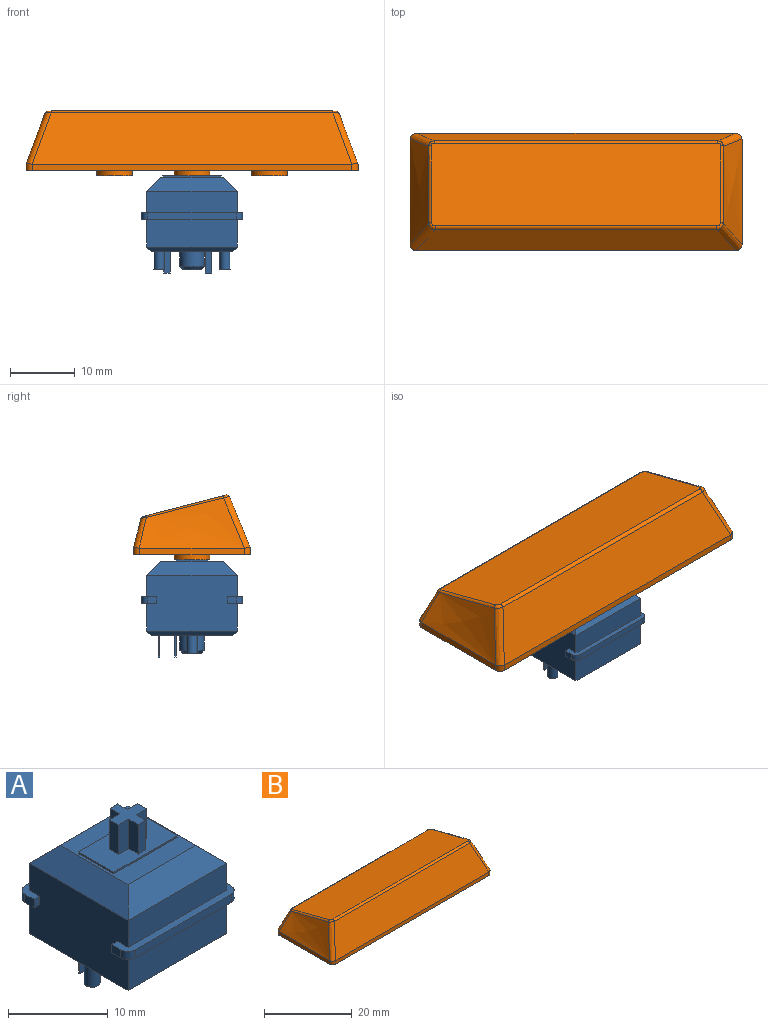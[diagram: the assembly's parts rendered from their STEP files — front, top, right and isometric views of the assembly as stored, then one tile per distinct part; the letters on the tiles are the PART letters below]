
ASSEMBLY  parts=2 mates=1
PART A: 69 faces, bbox 15.6x15.6x18.6 mm
  f0: plane 15.6x2.3mm, normal (0,0,-1), area 14.4mm2, adj f2,f3,f28,f30,f35,f60,f62,f63
  f1: plane 15.6x2.3mm, normal (0,0,-1), area 14.4mm2, adj f28,f30,f33,f34,f36,f59,f61,f64
  f2: plane 1.3x1mm, normal (1,0,0), area 1.3mm2, adj f0,f32,f62,f66
  f3: plane 1.3x1mm, normal (-1,0,0), area 1.3mm2, adj f0,f32,f63,f68
  f4: plane 15.6x2.3mm, normal (0,0,1), area 14.4mm2, adj f28,f30,f31,f33,f34,f36,f61,f64
  f5: plane 14x2.2mm, normal (-0.71,0,0.71), area 36.7mm2, adj f6,f7,f26,f30
  f6: plane 14x2.2mm, normal (0,-0.71,0.71), area 36.7mm2, adj f5,f7,f27,f31
  f7: plane 9.6x9.6mm, normal (0,0,1), area 47.2mm2, adj f5,f6,f8,f9,f10,f11,f26,f27
  f8: plane 5x0.2mm, normal (1,0,0), area 1mm2, adj f7,f9,f11,f12
  f9: plane 9x0.2mm, normal (0,1,0), area 1.8mm2, adj f7,f8,f10,f12
  f10: plane 5x0.2mm, normal (-1,0,0), area 1mm2, adj f7,f9,f11,f12
  f11: plane 9x0.2mm, normal (0,-1,0), area 1.8mm2, adj f7,f8,f10,f12
  f12: plane 9x5mm, normal (0,0,1), area 36.9mm2, adj f8,f9,f10,f11,f13,f14,f15,f16
  f13: plane 3.6x1.35mm, normal (1,0,0), area 4.9mm2, adj f12,f14,f24,f25
  f14: plane 3.6x1.08mm, normal (0,1,0), area 3.9mm2, adj f12,f13,f15,f25
  f15: plane 3.6x1.35mm, normal (-1,0,0), area 4.9mm2, adj f12,f14,f16,f25
  f16: plane 3.6x1.46mm, normal (0,1,0), area 5.3mm2, adj f12,f15,f17,f25
  f17: plane 3.6x1.3mm, normal (-1,0,0), area 4.7mm2, adj f12,f16,f18,f25
  f18: plane 3.6x1.46mm, normal (0,-1,0), area 5.3mm2, adj f12,f17,f19,f25
  f19: plane 3.6x1.35mm, normal (-1,0,0), area 4.9mm2, adj f12,f18,f20,f25
  f20: plane 3.6x1.08mm, normal (0,-1,0), area 3.9mm2, adj f12,f19,f21,f25
  f21: plane 3.6x1.35mm, normal (1,0,0), area 4.9mm2, adj f12,f20,f22,f25
  f22: plane 3.6x1.46mm, normal (0,-1,0), area 5.3mm2, adj f12,f21,f23,f25
  f23: plane 3.6x1.3mm, normal (1,0,0), area 4.7mm2, adj f12,f22,f24,f25
  f24: plane 3.6x1.46mm, normal (0,1,0), area 5.3mm2, adj f12,f13,f23,f25
  f25: plane 4x4mm, normal (0,0,1), area 8.1mm2, adj f13,f14,f15,f16,f17,f18,f19,f20
  f26: plane 14x2.2mm, normal (0,0.71,0.71), area 36.7mm2, adj f5,f7,f27,f29
  f27: plane 14x2.2mm, normal (0.71,0,0.71), area 36.7mm2, adj f6,f7,f26,f28
  f28: plane 14x8.6mm, normal (1,0,0), area 117.4mm2, adj f0,f1,f4,f27,f29,f31,f32,f55
  f29: plane 14x3.3mm, normal (0,1,0), area 46.2mm2, adj f26,f28,f30,f32
  f30: plane 14x8.6mm, normal (-1,0,0), area 117.4mm2, adj f0,f1,f4,f5,f29,f31,f32,f57
  f31: plane 14x3.3mm, normal (0,-1,0), area 46.2mm2, adj f4,f6,f28,f30
  f32: plane 15.6x2.3mm, normal (0,0,1), area 14.4mm2, adj f2,f3,f28,f29,f30,f35,f62,f63
  f33: plane 13.6x1mm, normal (0,-1,0), area 13.6mm2, adj f1,f4,f61,f64
  f34: plane 1.3x1mm, normal (1,0,0), area 1.3mm2, adj f1,f4,f61,f65
  f35: plane 13.6x1mm, normal (0,1,0), area 13.6mm2, adj f0,f32,f62,f63
  f36: plane 1.3x1mm, normal (-1,0,0), area 1.3mm2, adj f1,f4,f64,f67
  f37: plane 2.85x2.85mm, normal (0,0,-1), area 6.4mm2, adj f38
  f38: cone r=1.43mm half-angle=45deg, axis (0,0,1), area 7.4mm2, adj f37,f43
  f39: plane 1x0.2mm, normal (0,0,-1), area 0.2mm2, adj f44,f45,f46,f47
  f40: plane 1x0.2mm, normal (0,0,-1), area 0.2mm2, adj f48,f49,f50,f51
  f41: plane 1.6x1.6mm, normal (0,0,-1), area 2mm2, adj f52
  f42: plane 1.6x1.6mm, normal (0,0,-1), area 2mm2, adj f53
  f43: cylinder r=1.93mm len=3.85mm, axis (0,0,1), area 27.8mm2, adj f38,f54
  f44: plane 3.3x0.2mm, normal (-1,0,0), area 0.7mm2, adj f39,f45,f47,f54
  f45: plane 3.3x1mm, normal (0,1,0), area 3.3mm2, adj f39,f44,f46,f54
  f46: plane 3.3x0.2mm, normal (1,0,0), area 0.7mm2, adj f39,f45,f47,f54
  f47: plane 3.3x1mm, normal (0,-1,0), area 3.3mm2, adj f39,f44,f46,f54
  f48: plane 3.3x0.2mm, normal (-1,0,0), area 0.7mm2, adj f40,f49,f51,f54
  f49: plane 3.3x1mm, normal (0,1,0), area 3.3mm2, adj f40,f48,f50,f54
  f50: plane 3.3x0.2mm, normal (1,0,0), area 0.7mm2, adj f40,f49,f51,f54
  f51: plane 3.3x1mm, normal (0,-1,0), area 3.3mm2, adj f40,f48,f50,f54
  f52: cylinder r=0.8mm len=2.8mm, axis (0,0,1), area 14.1mm2, adj f41,f54
  f53: cylinder r=0.8mm len=2.8mm, axis (0,0,1), area 14.1mm2, adj f42,f54
  f54: plane 12.6x12.6mm, normal (0,0,-1), area 142.7mm2, adj f43,f44,f45,f46,f47,f48,f49,f50
  f55: plane 14x0.7mm, normal (0.71,0,-0.71), area 13.2mm2, adj f28,f54,f56,f58
  f56: plane 14x0.7mm, normal (0,0.71,-0.71), area 13.2mm2, adj f54,f55,f57,f60
  f57: plane 14x0.7mm, normal (-0.71,0,-0.71), area 13.2mm2, adj f30,f54,f56,f58
  f58: plane 14x0.7mm, normal (0,-0.71,-0.71), area 13.2mm2, adj f54,f55,f57,f59
  f59: plane 14x4.3mm, normal (0,-1,0), area 60.2mm2, adj f1,f28,f30,f58
  f60: plane 14x4.3mm, normal (0,1,0), area 60.2mm2, adj f0,f28,f30,f56
  f61: cylinder r=1mm len=1mm, axis (0,0,-1), area 1.6mm2, adj f1,f4,f33,f34
  f62: cylinder r=1mm len=1mm, axis (0,0,1), area 1.6mm2, adj f0,f2,f32,f35
  f63: cylinder r=1mm len=1mm, axis (0,0,-1), area 1.6mm2, adj f0,f3,f32,f35
  f64: cylinder r=1mm len=1mm, axis (0,0,1), area 1.6mm2, adj f1,f4,f33,f36
  f65: plane 1x0.8mm, normal (0,1,0), area 0.8mm2, adj f1,f4,f28,f34
  f66: plane 1x0.8mm, normal (0,-1,0), area 0.8mm2, adj f0,f2,f28,f32
  f67: plane 1x0.8mm, normal (0,1,0), area 0.8mm2, adj f1,f4,f30,f36
  f68: plane 1x0.8mm, normal (0,-1,0), area 0.8mm2, adj f0,f3,f30,f32
PART B: 80 faces, bbox 55.5x22.7x14.6 mm
  f0: plane 51.25x18.1mm, normal (0,0,-1), area 133.8mm2, adj f1,f2,f3,f4,f10,f12,f14,f16
  f1: plane 49.25x1mm, normal (0,-1,0), area 49.2mm2, adj f0,f8,f10,f12
  f2: plane 16.1x1mm, normal (1,0,0), area 16.1mm2, adj f0,f9,f10,f16
  f3: plane 49.25x1mm, normal (0,1,0), area 49.2mm2, adj f0,f6,f14,f15,f16,f17
  f4: plane 16.1x1mm, normal (-1,0,0), area 16.1mm2, adj f0,f7,f12,f14
  f5: plane 44.71x12.77mm, normal (0,0.25,0.97), area 588.2mm2, adj f18,f19,f20,f21,f22,f23,f24,f25
  f6: plane 49.21x4.53mm, normal (0,0.97,0.25), area 217.3mm2, adj f3,f15,f17,f20
  f7: bspline ~18.1x8.31mm, area 98.6mm2, adj f4,f12,f13,f14,f15,f19
  f8: plane 49.4x7.9mm, normal (0,-0.93,0.38), area 396.6mm2, adj f1,f10,f11,f12,f13,f23
  f9: bspline ~18.1x8.31mm, area 98.6mm2, adj f2,f10,f11,f16,f17,f24
  f10: cylinder r=1mm len=1.07mm, axis (0,0,1), area 1.6mm2, adj f0,f1,f2,f8,f9,f11
  f11: bspline ~11.3x5.51mm, area 13.2mm2, adj f8,f9,f10,f25
  f12: cylinder r=1mm len=1.07mm, axis (0,0,-1), area 1.6mm2, adj f0,f1,f4,f7,f8,f13
  f13: bspline ~11.44x5.57mm, area 13.2mm2, adj f7,f8,f12,f21
  f14: cylinder r=1mm len=1.01mm, axis (0,0,1), area 1.6mm2, adj f0,f3,f4,f7,f15
  f15: bspline ~7.23x4.95mm, area 7.7mm2, adj f3,f6,f7,f14,f18
  f16: cylinder r=1mm len=1.01mm, axis (0,0,-1), area 1.6mm2, adj f0,f2,f3,f9,f17
  f17: bspline ~7.14x4.9mm, area 7.7mm2, adj f3,f6,f9,f16,f22
  f18: bspline ~1.16x0.9mm, area 0.5mm2, adj f5,f15,f19,f20
  f19: bspline ~18.2x4.87mm, area 7mm2, adj f5,f7,f18,f21
  f20: cylinder r=0.5mm len=43.83mm, axis (-1,0,0), area 23.4mm2, adj f5,f6,f18,f22
  f21: bspline ~1.24x1.04mm, area 0.8mm2, adj f5,f13,f19,f23
  f22: bspline ~1.09x0.94mm, area 0.5mm2, adj f5,f17,f20,f24
  f23: cylinder r=0.5mm len=43.53mm, axis (-1,0,0), area 31.3mm2, adj f5,f8,f21,f25
  f24: bspline ~15.84x4.3mm, area 7mm2, adj f5,f9,f22,f25
  f25: bspline ~1.22x1.1mm, area 0.8mm2, adj f5,f11,f23,f24
  f26: plane 49.25x0.81mm, normal (0,1,0), area 39.6mm2, adj f0,f27,f29,f33
  f27: plane 16.18x0.9mm, normal (-1,0,0), area 12.4mm2, adj f0,f26,f28,f34
  f28: plane 49.25x0.87mm, normal (0,-1,0), area 43mm2, adj f0,f27,f29,f31,f32,f34
  f29: plane 16.18x0.9mm, normal (1,0,0), area 12.4mm2, adj f0,f26,f28,f32
  f30: plane 47.02x14.91mm, normal (0,-0.25,-0.97), area 474.1mm2, adj f31,f32,f33,f34,f46,f61,f76
  f31: plane 49.08x4.13mm, normal (0,-0.97,-0.25), area 198.1mm2, adj f28,f30,f32,f34
  f32: offset ~20.1x10.31mm, area 90.9mm2, adj f28,f29,f30,f31,f33
  f33: plane 49.3x7.36mm, normal (0,0.93,-0.38), area 367.8mm2, adj f26,f30,f32,f34
  f34: offset ~20.1x10.31mm, area 90.8mm2, adj f27,f28,f30,f31,f33
  f35: plane 7.77x1.5mm, normal (0,1,0), area 11.7mm2, adj f36,f44,f45,f49
  f36: plane 7.77x1.3mm, normal (1,0,0), area 9.9mm2, adj f35,f37,f45,f49
  f37: plane 7.44x1.5mm, normal (0,-1,0), area 11.2mm2, adj f36,f38,f45,f49
  f38: plane 7.44x1.35mm, normal (1,0,0), area 9.8mm2, adj f37,f39,f45,f49
  f39: plane 7.09x1mm, normal (0,-1,0), area 7.1mm2, adj f38,f40,f45,f49
  f40: plane 7.44x1.35mm, normal (-1,0,0), area 9.8mm2, adj f39,f41,f45,f49
  f41: plane 7.44x1.5mm, normal (0,-1,0), area 11.2mm2, adj f40,f42,f45,f49
  f42: plane 7.77x1.3mm, normal (-1,0,0), area 9.9mm2, adj f41,f43,f45,f49
  f43: plane 7.77x1.5mm, normal (0,1,0), area 11.7mm2, adj f42,f45,f47,f49
  f44: plane 8.12x1.35mm, normal (1,0,0), area 10.7mm2, adj f35,f45,f48,f49
  f45: plane 5.5x5.5mm, normal (0,0,-1), area 15.9mm2, adj f35,f36,f37,f38,f39,f40,f41,f42
  f46: cylinder r=2.75mm len=6.89mm, axis (0,0,-1), area 119.1mm2, adj f30,f45
  f47: plane 8.12x1.35mm, normal (-1,0,0), area 10.7mm2, adj f43,f45,f48,f49
  f48: plane 8.12x1mm, normal (0,1,0), area 8.1mm2, adj f44,f45,f47,f49
  f49: plane 4x4mm, normal (0,-0.25,-0.97), area 8.2mm2, adj f35,f36,f37,f38,f39,f40,f41,f42
  f50: plane 7.77x1.3mm, normal (-1,0,0), area 9.9mm2, adj f51,f59,f60,f64
  f51: plane 7.77x1.5mm, normal (0,1,0), area 11.7mm2, adj f50,f52,f60,f64
  f52: plane 8.12x1.35mm, normal (-1,0,0), area 10.7mm2, adj f51,f53,f60,f64
  f53: plane 8.12x1mm, normal (0,1,0), area 8.1mm2, adj f52,f54,f60,f64
  f54: plane 8.12x1.35mm, normal (1,0,0), area 10.7mm2, adj f53,f55,f60,f64
  f55: plane 7.77x1.5mm, normal (0,1,0), area 11.7mm2, adj f54,f56,f60,f64
  f56: plane 7.77x1.3mm, normal (1,0,0), area 9.9mm2, adj f55,f57,f60,f64
  f57: plane 7.44x1.5mm, normal (0,-1,0), area 11.2mm2, adj f56,f58,f60,f64
  f58: plane 7.44x1.35mm, normal (1,0,0), area 9.8mm2, adj f57,f60,f62,f64
  f59: plane 7.44x1.5mm, normal (0,-1,0), area 11.2mm2, adj f50,f60,f63,f64
  f60: plane 5.5x5.5mm, normal (0,0,-1), area 15.9mm2, adj f50,f51,f52,f53,f54,f55,f56,f57
  f61: cylinder r=2.75mm len=6.89mm, axis (0,0,-1), area 119.1mm2, adj f30,f60
  f62: plane 7.09x1mm, normal (0,-1,0), area 7.1mm2, adj f58,f60,f63,f64
  f63: plane 7.44x1.35mm, normal (-1,0,0), area 9.8mm2, adj f59,f60,f62,f64
  f64: plane 4x4mm, normal (0,-0.25,-0.97), area 8.2mm2, adj f50,f51,f52,f53,f54,f55,f56,f57
  f65: plane 7.77x1.3mm, normal (-1,0,0), area 9.9mm2, adj f66,f74,f75,f79
  f66: plane 7.77x1.5mm, normal (0,1,0), area 11.7mm2, adj f65,f67,f75,f79
  f67: plane 8.12x1.35mm, normal (-1,0,0), area 10.7mm2, adj f66,f68,f75,f79
  f68: plane 8.12x1mm, normal (0,1,0), area 8.1mm2, adj f67,f69,f75,f79
  f69: plane 8.12x1.35mm, normal (1,0,0), area 10.7mm2, adj f68,f70,f75,f79
  f70: plane 7.77x1.5mm, normal (0,1,0), area 11.7mm2, adj f69,f71,f75,f79
  f71: plane 7.77x1.3mm, normal (1,0,0), area 9.9mm2, adj f70,f72,f75,f79
  f72: plane 7.44x1.5mm, normal (0,-1,0), area 11.2mm2, adj f71,f73,f75,f79
  f73: plane 7.44x1.35mm, normal (1,0,0), area 9.8mm2, adj f72,f75,f77,f79
  f74: plane 7.44x1.5mm, normal (0,-1,0), area 11.2mm2, adj f65,f75,f78,f79
  f75: plane 5.5x5.5mm, normal (0,0,-1), area 15.9mm2, adj f65,f66,f67,f68,f69,f70,f71,f72
  f76: cylinder r=2.75mm len=6.89mm, axis (0,0,-1), area 119.1mm2, adj f30,f75
  f77: plane 7.09x1mm, normal (0,-1,0), area 7.1mm2, adj f73,f75,f78,f79
  f78: plane 7.44x1.35mm, normal (-1,0,0), area 9.8mm2, adj f74,f75,f77,f79
  f79: plane 4x4mm, normal (0,-0.25,-0.97), area 8.2mm2, adj f65,f66,f67,f68,f69,f70,f71,f72
PLACE A at identity fixed
PLACE B t=(0,0,11.7)mm
MATE fastened B.f46 <-> A.f38  axis (0,0,-1) through (0,0,11.7)mm
